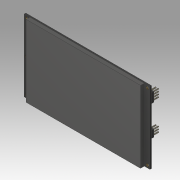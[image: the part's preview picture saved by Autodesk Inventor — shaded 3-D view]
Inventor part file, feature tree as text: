
AUTODESK INVENTOR PART (.ipt)
format: ipt  version: 2019.3 (Build 233278000, 278)  size: 387,584 bytes
history: native  units: mm
features: extrude x10, sketch x10, projected_geometry x6
ambient origin geometry x8: Origin, YZ Plane, XZ Plane, XY Plane, X Axis, Y Axis, Z Axis, Center Point
bodies: Solid1 (feature_tree)
feature tree (26):
  extrude  "Extrusion1"  Depth=76.0mm
  extrude  "Extrusion2"  Depth=70.6mm
  extrude  "Extrusion3"  Depth=2.7mm
  extrude  "Extrusion4"  Depth=2.7mm
  extrude  "Extrusion5"  Depth=1.6mm TaperAngle=0.0deg
  extrude  "Extrusion6"  Depth=75.999mm
  extrude  "Extrusion7"  Depth=4.0mm TaperAngle=0.0deg
  extrude  "Extrusion8"  Depth=7.5mm
  extrude  "Extrusion9"  Depth=10.0mm
  extrude  "Extrusion10"  Depth=24.5mm
  sketch  "Sketch1"  dims[d0=133.0mm d1=76.0mm]
  sketch  "Sketch2"  dims[d2=3.1mm d3=70.6mm]
  projected_geometry  "Projected Loop1"
  sketch  "Sketch3"  dims[d4=127.6mm d5=2.7mm]
  sketch  "Sketch4"  dims[d6=2.7mm d7=2.7mm]
  sketch  "Sketch5"  dims[d8=2.7mm d9=1.6mm d10=0.0mm]
  sketch  "Sketch6"  dims[d11=121.0mm d12=75.999mm]
  sketch  "Sketch7"  dims[d13=6.0mm d14=4.0mm d15=0.0mm]
  sketch  "Sketch8"  dims[d16=5.0mm d17=7.5mm]
  projected_geometry  "Projected Loop2"
  projected_geometry  "Projected Loop3"
  projected_geometry  "Projected Loop4"
  projected_geometry  "Projected Loop5"
  sketch  "Sketch9"  dims[d18=5.0mm d19=10.0mm]
  projected_geometry  "Projected Loop6"
  sketch  "Sketch10"  dims[d20=6.5mm d21=24.5mm d22=27.5mm d23=0.01mm d24=2.5mm d25=0.0mm d26=20.0mm d28=2.54mm d29=40.0mm d31=2.54mm d34=0.815mm d35=0.75mm d36=0.75mm d37=0.855mm d38=0.855mm d39=0.815mm d40=20.0mm d42=2.54mm d43=30.0mm d45=2.54mm d48=0.86mm d49=0.81mm d50=6.0mm d51=0.0mm d52=14.0mm d53=14.0mm d54=24.0mm d55=39.0mm d56=1.4mm d57=0.0mm d58=6.1mm d59=10.0mm d60=5.0mm d61=22.0mm d62=6.0mm d63=0.0mm d64=13.0mm d65=36.0mm d66=4.0mm d67=16.0mm d68=7.0mm d69=2.5mm d70=10.5mm d71=7.0mm d72=2.5mm d73=0.0mm d74=1.3mm d75=15.0mm d76=37.0mm d77=2.45mm d78=0.0mm d79=3.5mm d80=10.0mm d81=23.0mm d82=36.0mm d83=3.5mm d84=0.0mm d85=24.5mm d86=29.0mm d87=29.0mm d88=25.5mm d89=15.0mm d90=15.0mm d91=3.5mm d92=18.0mm d93=2.0mm d94=0.0mm]
